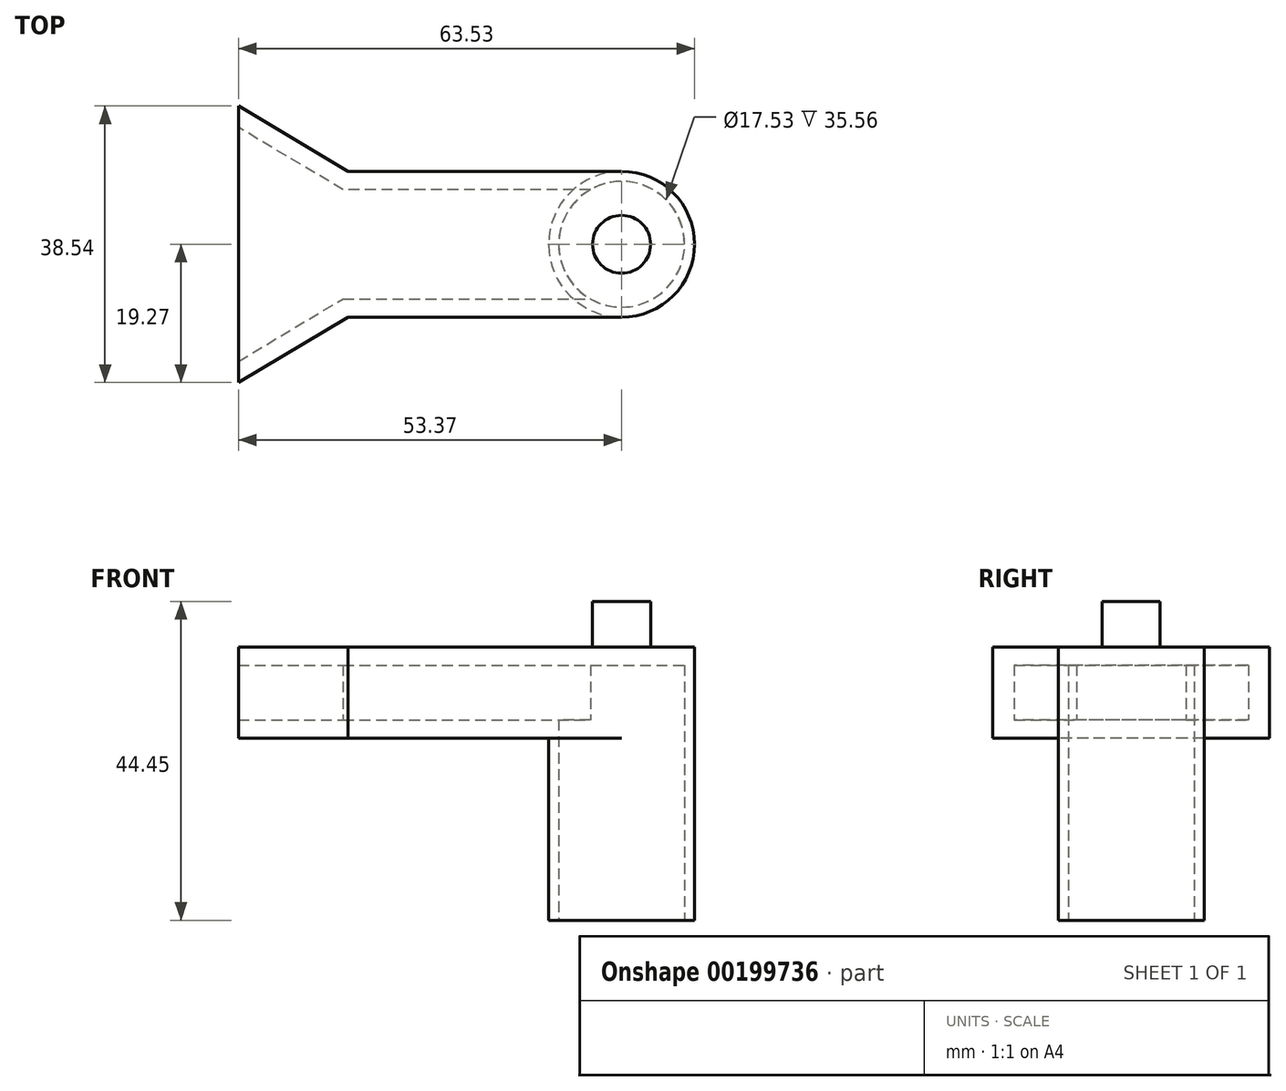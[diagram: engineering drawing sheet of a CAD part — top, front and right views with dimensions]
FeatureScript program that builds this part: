
annotation { "Feature Type Name" : "Feature", "Feature Type Description" : "" }
export const myFeature = defineFeature(function(context is Context, id is Id, definition is map)
    precondition{}
    {
        {
            var Q0;
            Q0=qCreatedBy(makeId("Top.planeOp"),FACE);
            var sketch = newSketch(context, id + "F0", { "sketchPlane" : qUnion([Q0])});
            skCircle(sketch, "E0", {"center": v(0, 0) * mm, "radius": 8.76 * mm});
            skCircle(sketch, "E1", {"center": v(0, 0) * mm, "radius": 10.16 * mm});
            skSolve(sketch);
        }
        {
            var Q0;
            Q0 = qSketchRegion(id + "F0", true);
            extrude(context, id + "F1", {"entities" : qUnion([Q0]), "depth" : 25.4 * mm});
        }
        {
            var Q0;
            Q0=makeQuery(id+"F1.opExtrude","CAP_FACE",FACE,{"disambiguationData":[OSD([sQuery(id+"F0.wireOp",EDGE,"E0"),sQuery(id+"F0.wireOp",EDGE,"E1")])],"isStart":false});
            cPlane(context, id + "F2", {"entities" : qUnion([Q0]), "cplaneType" : CPlaneType.OFFSET, "offset" : 0 * mm, "width" : 152.4 * mm, "height" : 152.4 * mm});
        }
        {
            var Q0;
            Q0=qCreatedBy(id+"F2.planeOp",FACE);
            var sketch = newSketch(context, id + "F3", { "sketchPlane" : qUnion([Q0])});
            skLineSegment(sketch, "E2", {"start": v(0, 0) * mm, "end": v(0, 10.16) * mm});
            skLineSegment(sketch, "E3", {"start": v(0, 10.16) * mm, "end": v(-38.1, 10.16) * mm});
            skLineSegment(sketch, "E4", {"start": v(-38.1, -10.16) * mm, "end": v(0, -10.16) * mm});
            skArc(sketch, "E5", {"start": v(0, 10.16) * mm, "mid": v(10.16, 0) * mm, "end": v(0, -10.16) * mm});
            skLineSegment(sketch, "E6", {"start": v(-38.1, 10.16) * mm, "end": v(-53.37, 19.27) * mm});
            skLineSegment(sketch, "E7", {"start": v(-53.37, 19.27) * mm, "end": v(-53.37, -19.27) * mm});
            skLineSegment(sketch, "E8", {"start": v(-53.37, -19.27) * mm, "end": v(-38.1, -10.16) * mm});
            skSolve(sketch);
        }
        {
            var Q0;
            Q0=makeQuery(id+"F3.imprint","IMPRINT",FACE,{"disambiguationData":[TD([[makeQuery(id+"F3.imprint","IMPRINT",EDGE,{"derivedFrom":sQuery(id+"F3.wireOp",EDGE,"E3")}),1.0]])]});
            extrude(context, id + "F4", {"entities" : qUnion([Q0]), "operationType" : NewBodyOperationType.ADD, "depth" : 12.7 * mm});
        }
        {
            var Q0;
            Q0=makeQuery(id+"F4.opExtrude","SWEPT_FACE",FACE,{"disambiguationData":[OSD([sQuery(id+"F3.wireOp",EDGE,"E7")])]});
            shell(context, id + "F5", {"entities" : qUnion([Q0]), "thickness" : 2.54 * mm});
        }
        {
            var Q0;
            Q0=makeQuery(id+"F4.boolean.opBoolean","SPLIT",FACE,{"disambiguationData":[TD([makeQuery(id+"F1.opExtrude","SWEPT_FACE",FACE,{"disambiguationData":[OSD([sQuery(id+"F0.wireOp",EDGE,"E0")])]})])],"derivedFrom":makeQuery(id+"F4.opExtrude","CAP_FACE",FACE,{"disambiguationData":[OSD([sQuery(id+"F3.wireOp",EDGE,"E3"),sQuery(id+"F3.wireOp",EDGE,"E4"),sQuery(id+"F3.wireOp",EDGE,"E5"),sQuery(id+"F3.wireOp",EDGE,"E6"),sQuery(id+"F3.wireOp",EDGE,"E7"),sQuery(id+"F3.wireOp",EDGE,"E8")])],"isStart":true})});
            extrude(context, id + "F6", {"entities" : qUnion([Q0]), "operationType" : NewBodyOperationType.REMOVE, "oppositeDirection" : true, "depth" : 10.16 * mm});
        }
        {
            var Q0;
            Q0=makeQuery(id+"F4.opExtrude","CAP_FACE",FACE,{"disambiguationData":[OSD([sQuery(id+"F3.wireOp",EDGE,"E3"),sQuery(id+"F3.wireOp",EDGE,"E4"),sQuery(id+"F3.wireOp",EDGE,"E5"),sQuery(id+"F3.wireOp",EDGE,"E6"),sQuery(id+"F3.wireOp",EDGE,"E7"),sQuery(id+"F3.wireOp",EDGE,"E8")])],"isStart":false});
            cPlane(context, id + "F7", {"entities" : qUnion([Q0]), "cplaneType" : CPlaneType.OFFSET, "offset" : 0 * mm, "width" : 152.4 * mm, "height" : 152.4 * mm});
        }
        {
            var Q0;
            Q0=qCreatedBy(id+"F7.planeOp",FACE);
            var sketch = newSketch(context, id + "F8", { "sketchPlane" : qUnion([Q0])});
            skCircle(sketch, "E9", {"center": v(0, 0) * mm, "radius": 4.04 * mm});
            skSolve(sketch);
        }
        {
            var Q0;
            Q0 = qSketchRegion(id + "F8", true);
            extrude(context, id + "F9", {"entities" : qUnion([Q0]), "operationType" : NewBodyOperationType.ADD, "depth" : 6.35 * mm});
        }
    });
